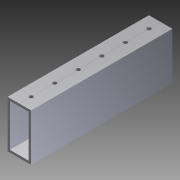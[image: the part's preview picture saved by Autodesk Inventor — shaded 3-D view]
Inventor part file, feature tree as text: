
AUTODESK INVENTOR PART (.ipt)
format: ipt  version: 2014 SP1 (Build 180222100, 222)  size: 634,880 bytes
history: native  units: in
note: dims shown in document units (in); Inventor stores cm internally (conversion verified against a paired STEP export)
features: other x2, extrude x1, imported_body x1, sketch x1
ambient origin geometry x8: Origin, YZ Plane, XZ Plane, XY Plane, X Axis, Y Axis, Z Axis, Center Point
bodies: Body1 (feature_tree)
feature tree (5):
  other  "Cut-Extrude2"
  other  "2x1 Tube1"
  extrude  "Extrusion1"  [1 undecoded]
  imported_body  "Base1"
  sketch  "Sketch1"  dims[d0=53.0in d1=0.0in]
note: 1 required parameter value undecoded (feature->parameter linkage not recoverable at this tier; creation-order binding heuristic only, values carry confidence <= 0.55)
